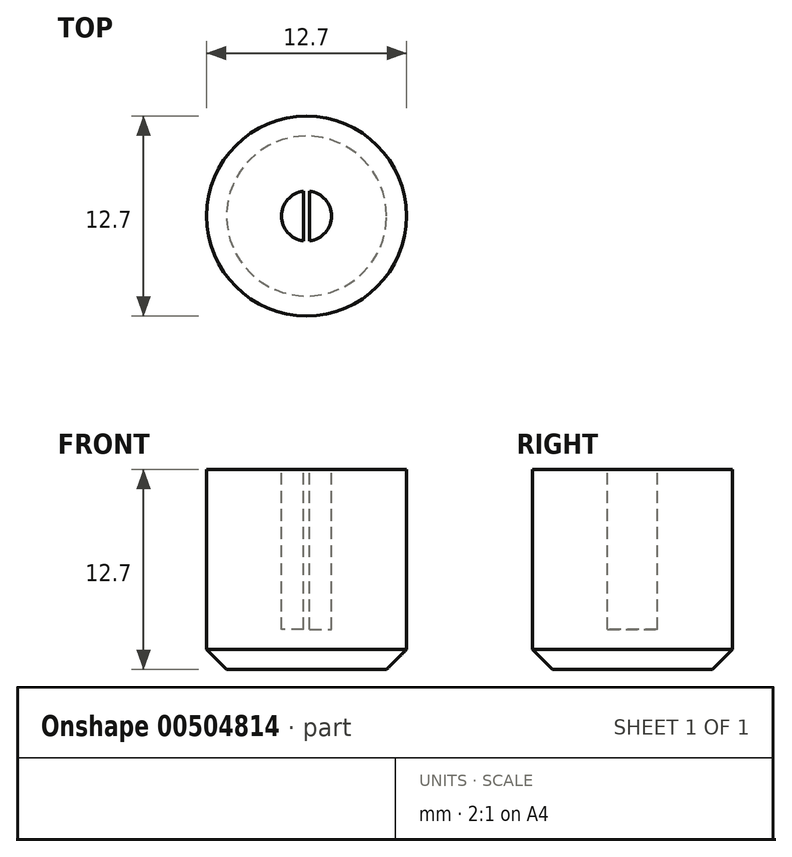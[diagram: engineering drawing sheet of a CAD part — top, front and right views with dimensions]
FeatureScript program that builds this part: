
annotation { "Feature Type Name" : "Feature", "Feature Type Description" : "" }
export const myFeature = defineFeature(function(context is Context, id is Id, definition is map)
    precondition{}
    {
        {
            var Q0;
            Q0=qCreatedBy(makeId("Top.planeOp"),FACE);
            var sketch = newSketch(context, id + "F0", { "sketchPlane" : qUnion([Q0])});
            skCircle(sketch, "E0", {"center": v(0, 0) * mm, "radius": 6.35 * mm});
            skSolve(sketch);
        }
        {
            var Q0;
            Q0 = qSketchRegion(id + "F0", true);
            extrude(context, id + "F1", {"entities" : qUnion([Q0]), "oppositeDirection" : true, "depth" : 12.7 * mm});
        }
        {
            var Q0;
            Q0=makeQuery(id+"F1.opExtrude","CAP_FACE",FACE,{"disambiguationData":[OSD([sQuery(id+"F0.wireOp",EDGE,"E0")])],"isStart":true});
            var sketch = newSketch(context, id + "F2", { "sketchPlane" : qUnion([Q0])});
            skCircle(sketch, "E1", {"center": v(0, 0) * mm, "radius": 1.59 * mm});
            skSolve(sketch);
        }
        {
            var Q0;
            Q0 = qSketchRegion(id + "F2", true);
            extrude(context, id + "F3", {"entities" : qUnion([Q0]), "operationType" : NewBodyOperationType.REMOVE, "oppositeDirection" : true, "depth" : 10.16 * mm});
        }
        {
            var Q0;
            Q0=qCreatedBy(makeId("Top.planeOp"),FACE);
            var sketch = newSketch(context, id + "F4", { "sketchPlane" : qUnion([Q0])});
            skLineSegment(sketch, "E2.bottom", {"start": v(0.2, 1.86) * mm, "end": v(-0.2, 1.86) * mm});
            skLineSegment(sketch, "E2.top", {"start": v(0.2, -1.86) * mm, "end": v(-0.2, -1.86) * mm});
            skLineSegment(sketch, "E2.left", {"start": v(0.2, 1.86) * mm, "end": v(0.2, -1.86) * mm});
            skLineSegment(sketch, "E2.right", {"start": v(-0.2, 1.86) * mm, "end": v(-0.2, -1.86) * mm});
            skPoint(sketch, "E2.middle", {"position": v(0, 0) * mm});
            skSolve(sketch);
        }
        {
            var Q0;
            Q0 = qSketchRegion(id + "F4", true);
            extrude(context, id + "F5", {"entities" : qUnion([Q0]), "operationType" : NewBodyOperationType.ADD, "oppositeDirection" : true, "depth" : 11.46 * mm});
        }
        {
            var Q0;
            Q0=makeQuery(id+"F1.opExtrude","CAP_EDGE",EDGE,{"disambiguationData":[OSD([sQuery(id+"F0.wireOp",EDGE,"E0")])],"isStart":false});
            chamfer(context, id + "F6", {"entities" : qUnion([Q0]), "width" : 1.27 * mm, "tangentPropagation" : true});
        }
    });
